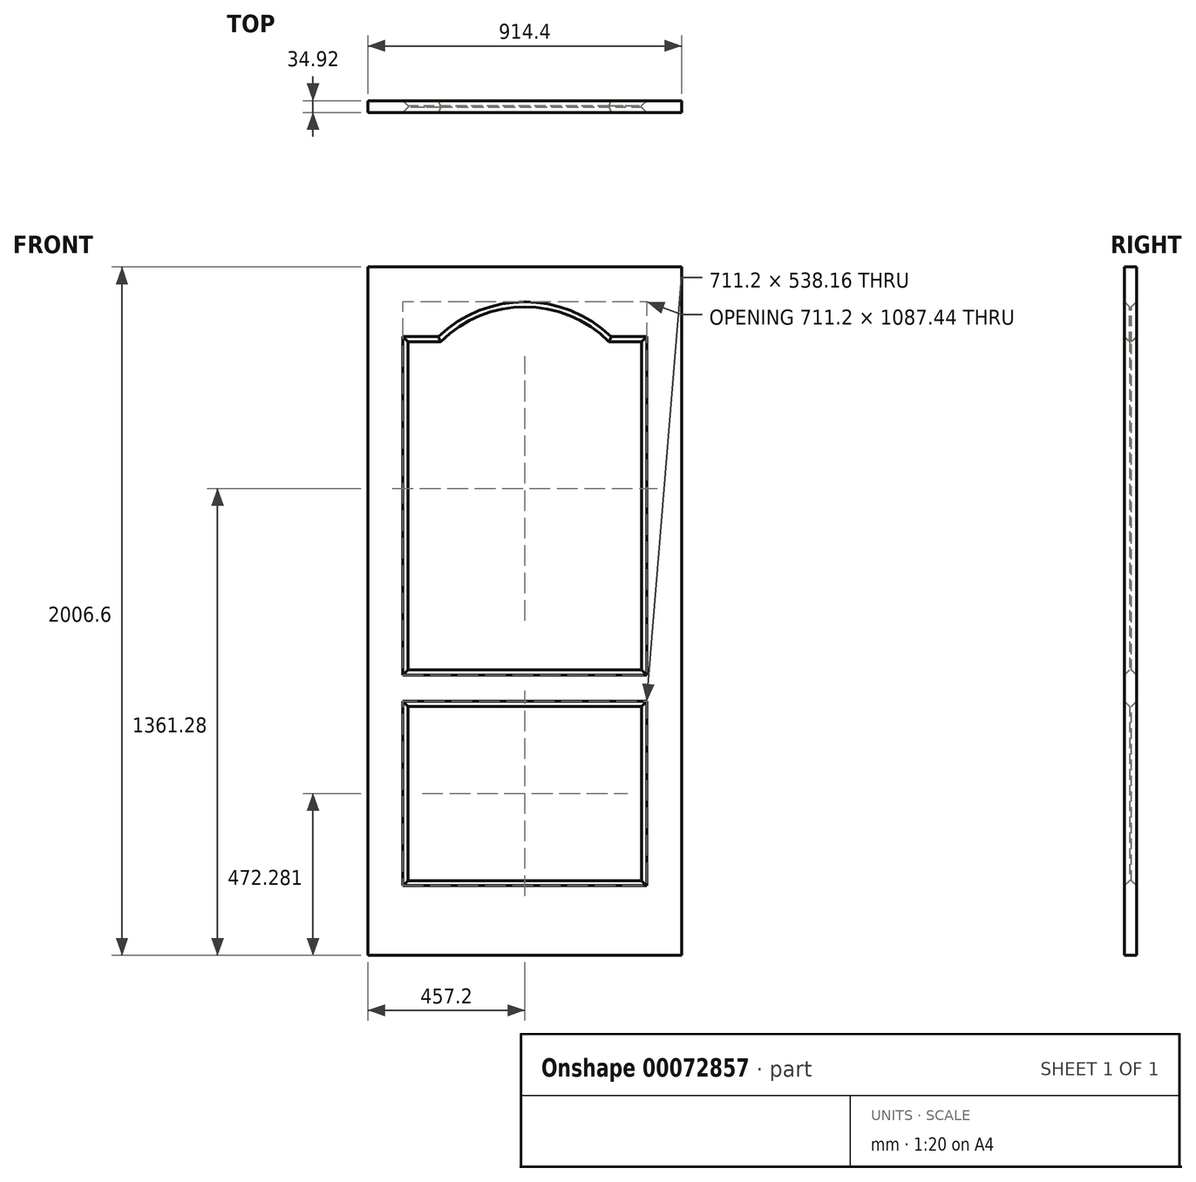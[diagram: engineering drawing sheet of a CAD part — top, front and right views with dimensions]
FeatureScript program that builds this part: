
annotation { "Feature Type Name" : "Feature", "Feature Type Description" : "" }
export const myFeature = defineFeature(function(context is Context, id is Id, definition is map)
    precondition{}
    {
        {
            var Q0;
            Q0=qCreatedBy(makeId("Front.planeOp"),FACE);
            var sketch = newSketch(context, id + "F0", { "sketchPlane" : qUnion([Q0])});
            skLineSegment(sketch, "E0.bottom", {"start": v(-457.2, 2006.6) * mm, "end": v(457.2, 2006.6) * mm});
            skLineSegment(sketch, "E0.top", {"start": v(-457.2, 0) * mm, "end": v(457.2, 0) * mm});
            skLineSegment(sketch, "E0.left", {"start": v(-457.2, 2006.6) * mm, "end": v(-457.2, 0) * mm});
            skLineSegment(sketch, "E0.right", {"start": v(457.2, 2006.6) * mm, "end": v(457.2, 0) * mm});
            skLineSegment(sketch, "E1", {"start": v(0, 0) * mm, "end": v(0, 2006.6) * mm, "construction": true});
            skLineSegment(sketch, "E2.top", {"start": v(-355.6, 817.56) * mm, "end": v(355.6, 817.56) * mm});
            skLineSegment(sketch, "E2.left", {"start": v(-355.6, 1803.4) * mm, "end": v(-355.6, 817.56) * mm});
            skLineSegment(sketch, "E2.right", {"start": v(355.6, 1803.4) * mm, "end": v(355.6, 817.56) * mm});
            skLineSegment(sketch, "E3.bottom", {"start": v(-355.6, 741.36) * mm, "end": v(355.6, 741.36) * mm});
            skLineSegment(sketch, "E3.top", {"start": v(-355.6, 203.2) * mm, "end": v(355.6, 203.2) * mm});
            skLineSegment(sketch, "E3.left", {"start": v(-355.6, 741.36) * mm, "end": v(-355.6, 203.2) * mm});
            skLineSegment(sketch, "E3.right", {"start": v(355.6, 741.36) * mm, "end": v(355.6, 203.2) * mm});
            skLineSegment(sketch, "E4", {"start": v(-355.6, 1803.4) * mm, "end": v(-251.68, 1803.4) * mm});
            skLineSegment(sketch, "E5.trimOffspring", {"start": v(251.68, 1803.4) * mm, "end": v(355.6, 1803.4) * mm});
            skArc(sketch, "E6.trimOffspring", {"start": v(251.68, 1803.4) * mm, "mid": v(0, 1905) * mm, "end": v(-251.68, 1803.4) * mm});
            skSolve(sketch);
        }
        {
            var Q0;
            Q0=makeQuery(id+"F0.imprint","IMPRINT",FACE,{"disambiguationData":[TD([[makeQuery(id+"F0.imprint","IMPRINT",EDGE,{"derivedFrom":sQuery(id+"F0.wireOp",EDGE,"E3.bottom")}),-1.0]])]});
            var Q1;
            Q1=makeQuery(id+"F0.imprint","IMPRINT",FACE,{"disambiguationData":[TD([[makeQuery(id+"F0.imprint","IMPRINT",EDGE,{"derivedFrom":sQuery(id+"F0.wireOp",EDGE,"b59e21e7-591d-4059-92ee-f49c818a9173.bottom")}),-1.0]])]});
            var Q2;
            Q2=makeQuery(id+"F0.imprint","IMPRINT",FACE,{"disambiguationData":[TD([[makeQuery(id+"F0.imprint","IMPRINT",EDGE,{"derivedFrom":sQuery(id+"F0.wireOp",EDGE,"E2.bottom")}),-1.0]])]});
            var Q3;
            Q3=makeQuery(id+"F0.imprint","IMPRINT",FACE,{"disambiguationData":[TD([[makeQuery(id+"F0.imprint","IMPRINT",EDGE,{"derivedFrom":sQuery(id+"F0.wireOp",EDGE,"E0.bottom")}),-1.0]])]});
            var Q4;
            Q4=makeQuery(id+"F0.imprint","IMPRINT",FACE,{"disambiguationData":[TD([[makeQuery(id+"F0.imprint","IMPRINT",EDGE,{"derivedFrom":sQuery(id+"F0.wireOp",EDGE,"E2.top")}),1.0]])]});
            extrude(context, id + "F1", {"entities" : qUnion([Q0, Q1, Q2, Q3, Q4]), "endBound" : BoundingType.SYMMETRIC, "offsetDistance" : 25.4 * mm, "depth" : 34.92 * mm});
        }
        {
            var Q0;
            Q0=makeQuery(id+"F1.opExtrude","CAP_FACE",FACE,{"disambiguationData":[OSD([sQuery(id+"F0.wireOp",EDGE,"E0.bottom"),sQuery(id+"F0.wireOp",EDGE,"E0.top"),sQuery(id+"F0.wireOp",EDGE,"E0.left"),sQuery(id+"F0.wireOp",EDGE,"E0.right")])],"isStart":true});
            var sketch = newSketch(context, id + "F2", { "sketchPlane" : qUnion([Q0])});
            skLineSegment(sketch, "E7.0", {"start": v(-355.6, 1803.4) * mm, "end": v(-355.6, 817.56) * mm});
            skLineSegment(sketch, "E8.0", {"start": v(355.6, 1803.4) * mm, "end": v(355.6, 817.56) * mm});
            skLineSegment(sketch, "E9.0", {"start": v(355.6, 817.56) * mm, "end": v(-355.6, 817.56) * mm});
            skLineSegment(sketch, "E10.0", {"start": v(355.6, 741.36) * mm, "end": v(-355.6, 741.36) * mm});
            skLineSegment(sketch, "E11.0", {"start": v(355.6, 741.36) * mm, "end": v(355.6, 203.2) * mm});
            skLineSegment(sketch, "E12.0", {"start": v(355.6, 203.2) * mm, "end": v(-355.6, 203.2) * mm});
            skLineSegment(sketch, "E13.0", {"start": v(-355.6, 741.36) * mm, "end": v(-355.6, 203.2) * mm});
            skLineSegment(sketch, "E14.0", {"start": v(-251.68, 1803.4) * mm, "end": v(-355.6, 1803.4) * mm});
            skArc(sketch, "E14.1", {"start": v(-251.68, 1803.4) * mm, "mid": v(0, 1905) * mm, "end": v(251.68, 1803.4) * mm});
            skLineSegment(sketch, "E14.2", {"start": v(355.6, 1803.4) * mm, "end": v(251.68, 1803.4) * mm});
            skSolve(sketch);
        }
        {
            var Q0;
            Q0=qSketchRegion(id+"F2",true);
            extrude(context, id + "F3", {"entities" : qUnion([Q0]), "operationType" : NewBodyOperationType.REMOVE, "oppositeDirection" : true, "depth" : 15.08 * mm, "hasDraft" : true, "draftAngle" : 45 * degree, "draftPullDirection" : true});
        }
        {
            var Q0;
            Q0=makeQuery(id+"F1.opExtrude","CAP_FACE",FACE,{"disambiguationData":[OSD([sQuery(id+"F0.wireOp",EDGE,"E0.bottom"),sQuery(id+"F0.wireOp",EDGE,"E0.top"),sQuery(id+"F0.wireOp",EDGE,"E0.left"),sQuery(id+"F0.wireOp",EDGE,"E0.right")])],"isStart":false});
            var sketch = newSketch(context, id + "F4", { "sketchPlane" : qUnion([Q0])});
            skLineSegment(sketch, "E15.0", {"start": v(-355.6, 1803.4) * mm, "end": v(-355.6, 817.56) * mm});
            skLineSegment(sketch, "E16.0", {"start": v(355.6, 1803.4) * mm, "end": v(355.6, 817.56) * mm});
            skLineSegment(sketch, "E17.0", {"start": v(-355.6, 817.56) * mm, "end": v(355.6, 817.56) * mm});
            skLineSegment(sketch, "E18.0", {"start": v(-355.6, 741.36) * mm, "end": v(355.6, 741.36) * mm});
            skLineSegment(sketch, "E19.0", {"start": v(355.6, 741.36) * mm, "end": v(355.6, 203.2) * mm});
            skLineSegment(sketch, "E20.0", {"start": v(-355.6, 741.36) * mm, "end": v(-355.6, 203.2) * mm});
            skLineSegment(sketch, "E21.0", {"start": v(-355.6, 203.2) * mm, "end": v(355.6, 203.2) * mm});
            skArc(sketch, "E22.0", {"start": v(251.68, 1803.4) * mm, "mid": v(0, 1905) * mm, "end": v(-251.68, 1803.4) * mm});
            skLineSegment(sketch, "E22.1", {"start": v(-355.6, 1803.4) * mm, "end": v(-251.68, 1803.4) * mm});
            skLineSegment(sketch, "E22.2", {"start": v(251.68, 1803.4) * mm, "end": v(355.6, 1803.4) * mm});
            skSolve(sketch);
        }
        {
            var Q0;
            Q0=qSketchRegion(id+"F4",true);
            extrude(context, id + "F5", {"entities" : qUnion([Q0]), "operationType" : NewBodyOperationType.REMOVE, "oppositeDirection" : true, "depth" : 15.08 * mm, "hasDraft" : true, "draftAngle" : 45 * degree, "draftPullDirection" : true});
        }
    });
